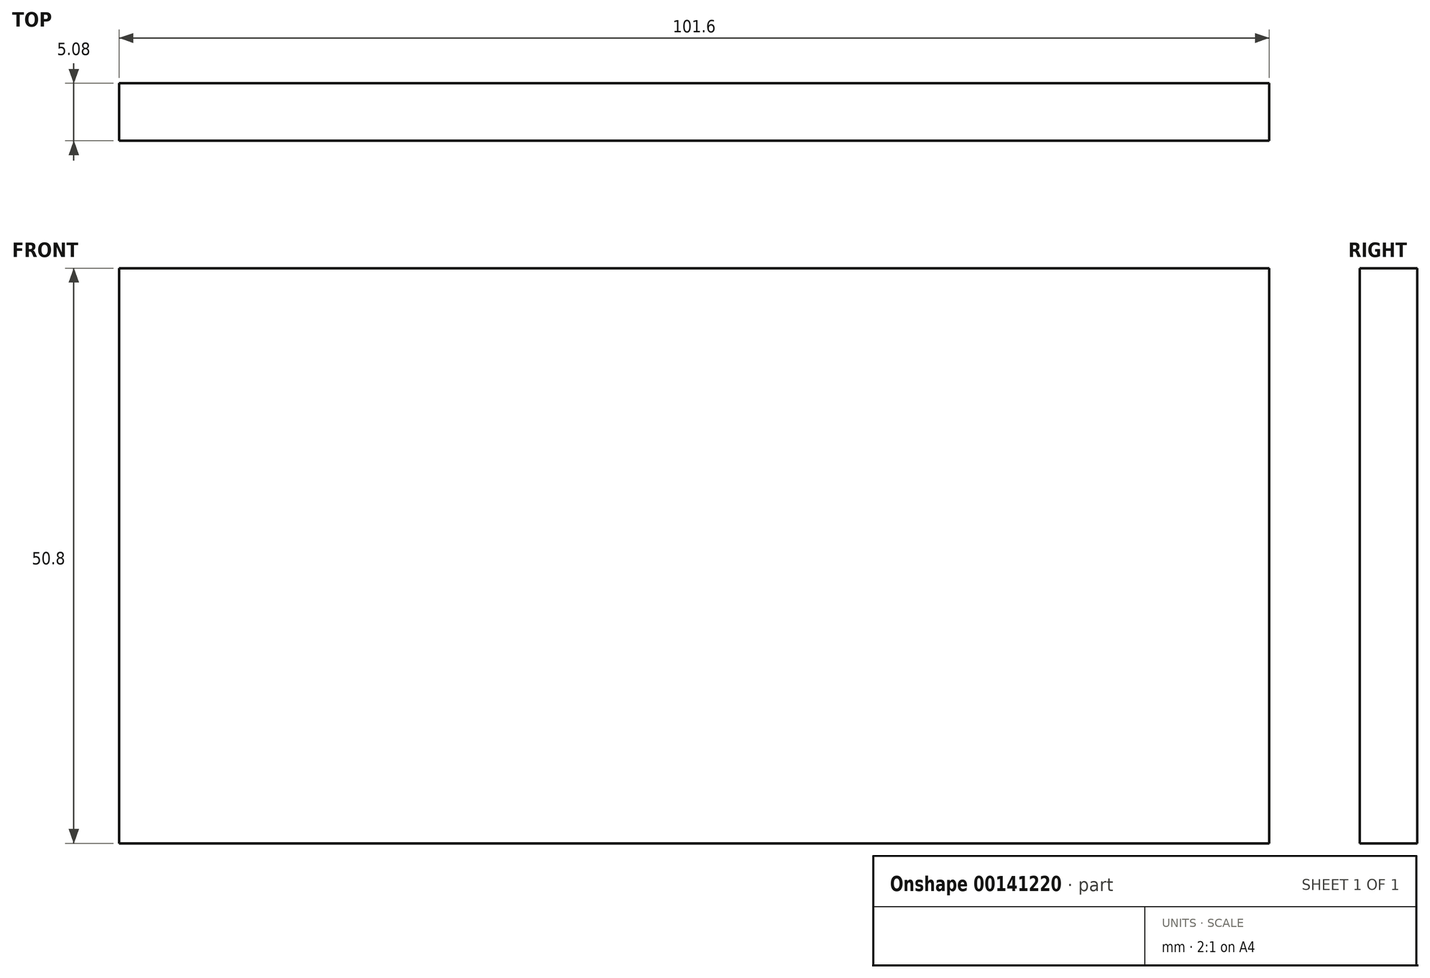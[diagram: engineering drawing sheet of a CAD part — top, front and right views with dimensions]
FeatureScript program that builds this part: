
annotation { "Feature Type Name" : "Feature", "Feature Type Description" : "" }
export const myFeature = defineFeature(function(context is Context, id is Id, definition is map)
    precondition{}
    {
        {
            var Q0;
            Q0=qCreatedBy(makeId("Front.planeOp"),FACE);
            var sketch = newSketch(context, id + "F0", { "sketchPlane" : qUnion([Q0])});
            skLineSegment(sketch, "E0.bottom", {"start": v(-20.32, 26.12) * mm, "end": v(81.28, 26.12) * mm});
            skLineSegment(sketch, "E0.top", {"start": v(-20.32, -24.68) * mm, "end": v(81.28, -24.68) * mm});
            skLineSegment(sketch, "E0.left", {"start": v(-20.32, 26.12) * mm, "end": v(-20.32, -24.68) * mm});
            skLineSegment(sketch, "E0.right", {"start": v(81.28, 26.12) * mm, "end": v(81.28, -24.68) * mm});
            skSolve(sketch);
        }
        {
            var Q0;
            Q0=makeQuery(id+"F0.imprint","IMPRINT",FACE,{"disambiguationData":[TD([[makeQuery(id+"F0.imprint","IMPRINT",EDGE,{"derivedFrom":sQuery(id+"F0.wireOp",EDGE,"E0.bottom")}),-1.0]])]});
            extrude(context, id + "F1", {"entities" : qUnion([Q0]), "depth" : 5.08 * mm});
        }
    });
